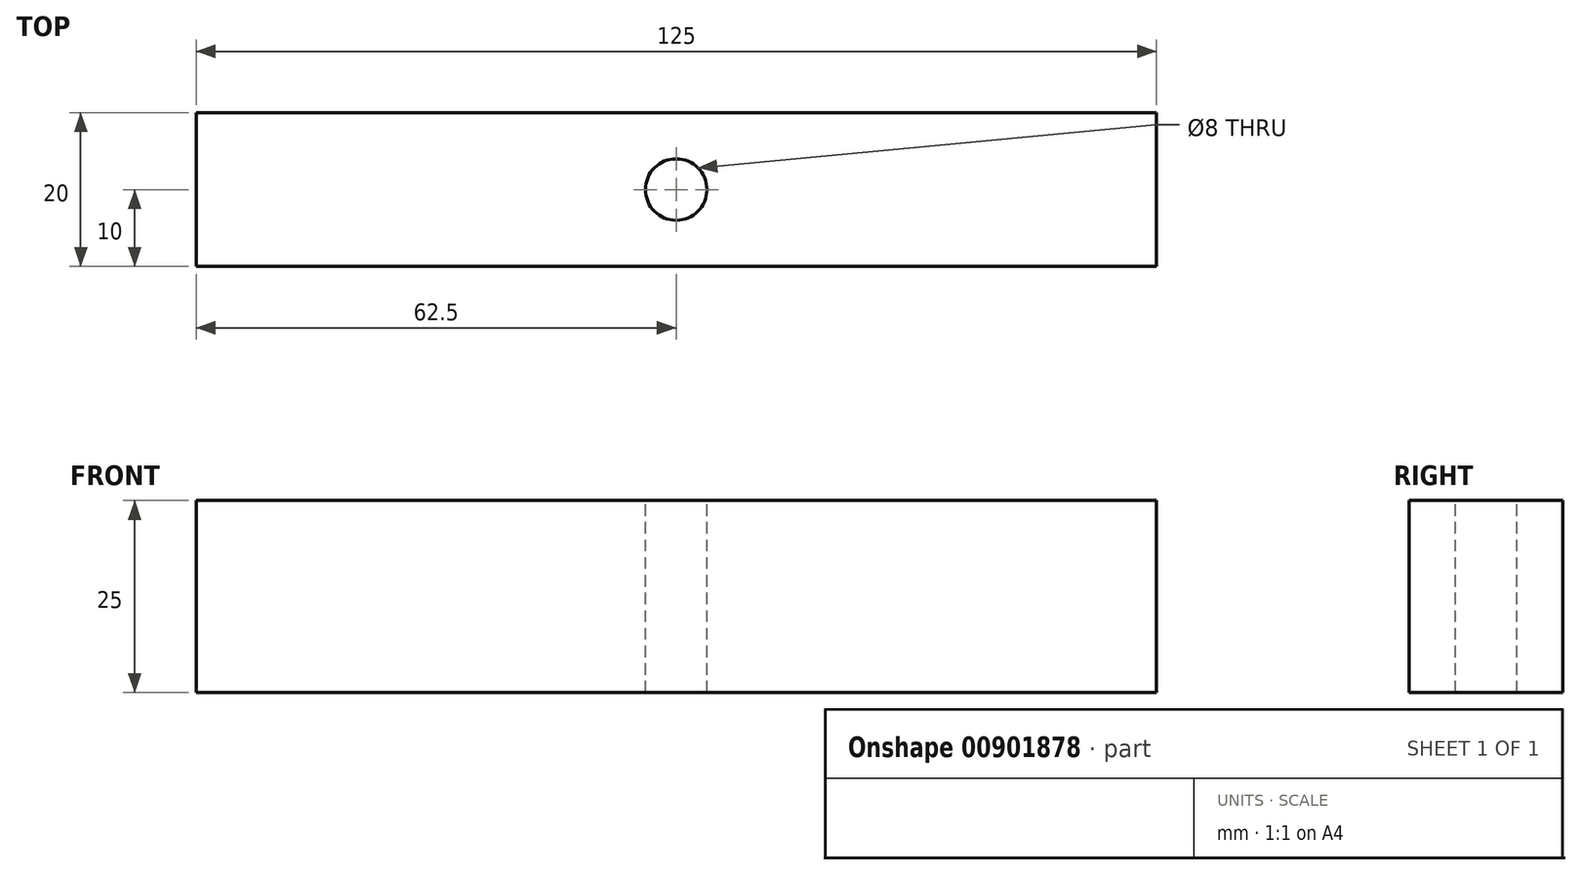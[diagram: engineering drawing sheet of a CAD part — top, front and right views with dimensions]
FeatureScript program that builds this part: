
annotation { "Feature Type Name" : "Feature", "Feature Type Description" : "" }
export const myFeature = defineFeature(function(context is Context, id is Id, definition is map)
    precondition{}
    {
        {
            var Q0;
            Q0=qCreatedBy(makeId("Front.planeOp"),FACE);
            var sketch = newSketch(context, id + "F0", { "sketchPlane" : qUnion([Q0])});
            skLineSegment(sketch, "E0.bottom", {"start": v(-62.5, 12.5) * mm, "end": v(62.5, 12.5) * mm});
            skLineSegment(sketch, "E0.top", {"start": v(-62.5, -12.5) * mm, "end": v(62.5, -12.5) * mm});
            skLineSegment(sketch, "E0.left", {"start": v(-62.5, 12.5) * mm, "end": v(-62.5, -12.5) * mm});
            skLineSegment(sketch, "E0.right", {"start": v(62.5, 12.5) * mm, "end": v(62.5, -12.5) * mm});
            skSolve(sketch);
        }
        {
            var Q0;
            Q0=makeQuery(id+"F0.imprint","IMPRINT",FACE,{"disambiguationData":[TD([[makeQuery(id+"F0.imprint","IMPRINT",EDGE,{"derivedFrom":sQuery(id+"F0.wireOp",EDGE,"E0.bottom")}),-1.0]])]});
            extrude(context, id + "F1", {"entities" : qUnion([Q0]), "depth" : 20 * mm, "offsetDistance" : 25 * mm, "symmetric" : true});
        }
        {
            var Q0;
            Q0=makeQuery(id+"F1.opExtrude","SWEPT_FACE",FACE,{"disambiguationData":[OSD([sQuery(id+"F0.wireOp",EDGE,"E0.bottom")])]});
            var sketch = newSketch(context, id + "F2", { "sketchPlane" : qUnion([Q0])});
            skCircle(sketch, "E1", {"center": v(0, 0) * mm, "radius": 4 * mm});
            skPoint(sketch, "E1.centerSnap0", {"position": v(0, 10) * mm});
            skSolve(sketch);
        }
        {
            var Q0;
            Q0=makeQuery(id+"F2.imprint","IMPRINT",FACE,{"disambiguationData":[TD([[makeQuery(id+"F2.imprint","IMPRINT",EDGE,{"derivedFrom":sQuery(id+"F2.wireOp",EDGE,"E1")}),1.0]])]});
            extrude(context, id + "F3", {"entities" : qUnion([Q0]), "operationType" : NewBodyOperationType.REMOVE, "oppositeDirection" : true, "depth" : 25 * mm, "offsetDistance" : 25 * mm});
        }
    });
